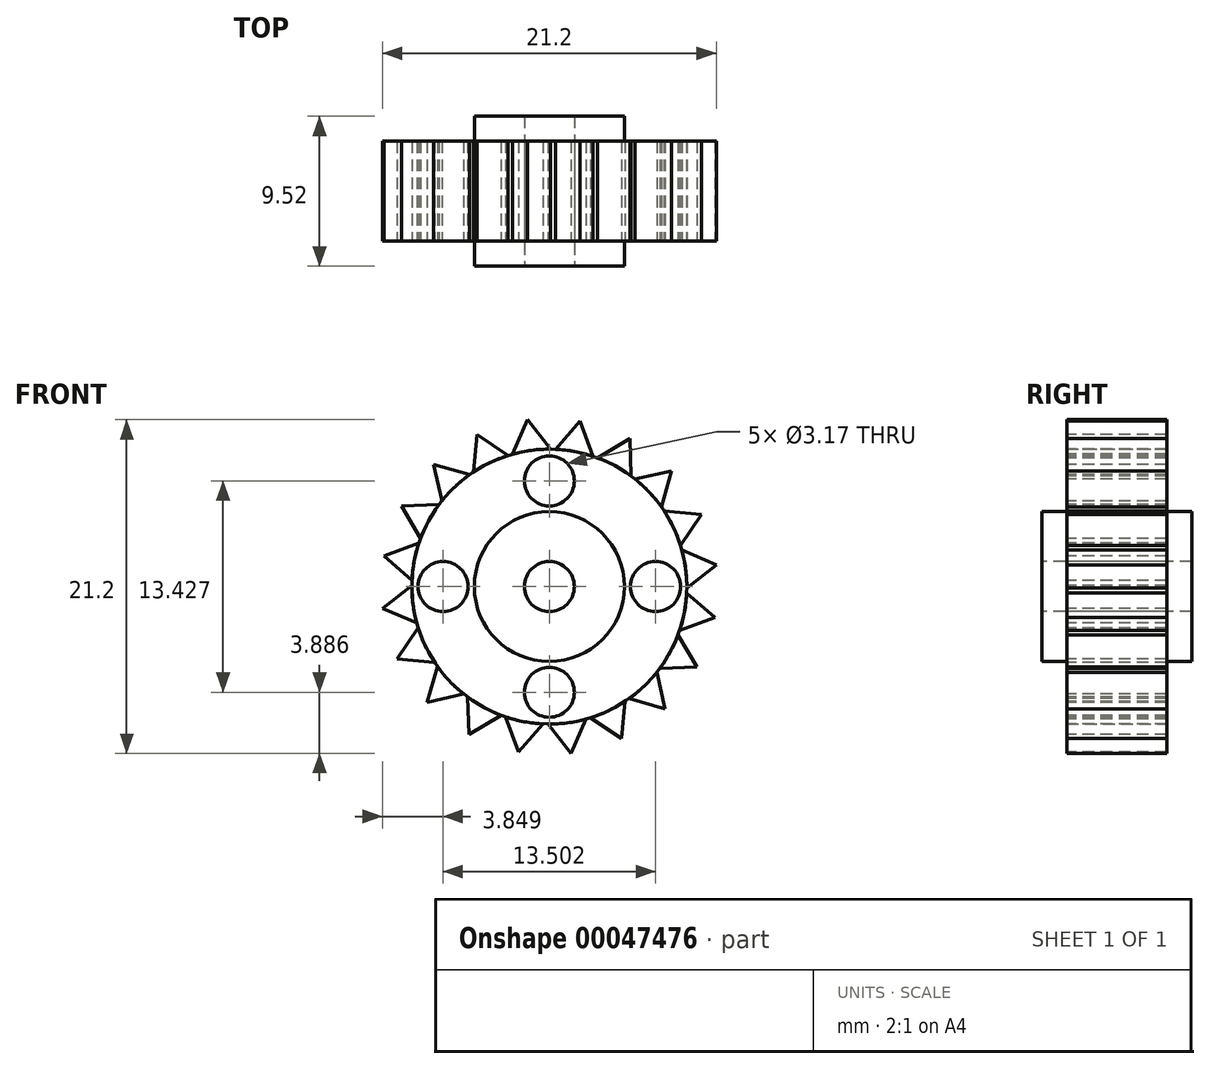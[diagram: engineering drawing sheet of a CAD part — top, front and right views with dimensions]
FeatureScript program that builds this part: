
annotation { "Feature Type Name" : "Feature", "Feature Type Description" : "" }
export const myFeature = defineFeature(function(context is Context, id is Id, definition is map)
    precondition{}
    {
        {
            var Q0;
            Q0=qCreatedBy(makeId("Front.planeOp"),FACE);
            var sketch = newSketch(context, id + "F0", { "sketchPlane" : qUnion([Q0])});
            skCircle(sketch, "E0", {"center": v(0, 0) * mm, "radius": 8.73 * mm});
            skSolve(sketch);
        }
        {
            var Q0;
            Q0=makeQuery(id+"F0.imprint","IMPRINT",FACE,{"disambiguationData":[TD([[makeQuery(id+"F0.imprint","IMPRINT",EDGE,{"derivedFrom":sQuery(id+"F0.wireOp",EDGE,"E0")}),1.0]])]});
            extrude(context, id + "F1", {"entities" : qUnion([Q0]), "depth" : 6.35 * mm, "symmetric" : true});
        }
        {
            var Q0;
            Q0=makeQuery(id+"F1.opExtrude","CAP_FACE",FACE,{"disambiguationData":[OSD([sQuery(id+"F0.wireOp",EDGE,"E0")])],"isStart":false});
            var sketch = newSketch(context, id + "F2", { "sketchPlane" : qUnion([Q0])});
            skCircle(sketch, "E1", {"center": v(0, 0) * mm, "radius": 4.76 * mm});
            skSolve(sketch);
        }
        {
            var Q0;
            Q0=makeQuery(id+"F2.imprint","IMPRINT",FACE,{"disambiguationData":[TD([[makeQuery(id+"F2.imprint","IMPRINT",EDGE,{"derivedFrom":sQuery(id+"F2.wireOp",EDGE,"E1")}),1.0]])]});
            extrude(context, id + "F3", {"entities" : qUnion([Q0]), "operationType" : NewBodyOperationType.ADD, "depth" : 1.59 * mm});
        }
        {
            var Q0;
            Q0=makeQuery(id+"F3.opExtrude","CAP_FACE",FACE,{"disambiguationData":[OSD([sQuery(id+"F2.wireOp",EDGE,"E1")])],"isStart":false});
            var sketch = newSketch(context, id + "F4", { "sketchPlane" : qUnion([Q0])});
            skCircle(sketch, "E2", {"center": v(0, 0) * mm, "radius": 1.59 * mm});
            skSolve(sketch);
        }
        {
            var Q0;
            Q0=makeQuery(id+"F4.imprint","IMPRINT",FACE,{"disambiguationData":[TD([[makeQuery(id+"F4.imprint","IMPRINT",EDGE,{"derivedFrom":sQuery(id+"F4.wireOp",EDGE,"E2")}),1.0]])]});
            extrude(context, id + "F5", {"entities" : qUnion([Q0]), "operationType" : NewBodyOperationType.REMOVE, "endBound" : BoundingType.THROUGH_ALL, "oppositeDirection" : true, "depth" : 25.4 * mm});
        }
        {
            var Q0;
            Q0=makeQuery(id+"F1.opExtrude","CAP_FACE",FACE,{"disambiguationData":[OSD([sQuery(id+"F0.wireOp",EDGE,"E0")])],"isStart":false});
            var sketch = newSketch(context, id + "F6", { "sketchPlane" : qUnion([Q0])});
            skCircle(sketch, "E3", {"center": v(0, 6.71) * mm, "radius": 1.59 * mm});
            skCircle(sketch, "E4.MirrorC", {"center": v(0, -6.71) * mm, "radius": 1.59 * mm});
            skCircle(sketch, "E5", {"center": v(-6.75, 0) * mm, "radius": 1.59 * mm});
            skCircle(sketch, "E6.MirrorC", {"center": v(6.75, 0) * mm, "radius": 1.59 * mm});
            skSolve(sketch);
        }
        {
            var Q0;
            Q0 = qSketchRegion(id + "F6", true);
            extrude(context, id + "F7", {"entities" : qUnion([Q0]), "operationType" : NewBodyOperationType.REMOVE, "endBound" : BoundingType.THROUGH_ALL, "oppositeDirection" : true, "depth" : 25.4 * mm});
        }
        {
            var Q0;
            Q0=makeQuery(id+"F1.opExtrude","SWEPT_BODY",BODY,{"disambiguationData":[OSD([sQuery(id+"F0.wireOp",EDGE,"E0")])]});
            var Q1;
            Q1=qCreatedBy(makeId("Front.planeOp"),FACE);
            mirror(context, id + "F8", {"operationType" : NewBodyOperationType.ADD, "entities" : qUnion([Q0]), "mirrorPlane" : qUnion([Q1])});
        }
        {
            var Q0;
            Q0=makeQuery(id+"F1.opExtrude","CAP_FACE",FACE,{"disambiguationData":[OSD([sQuery(id+"F0.wireOp",EDGE,"E0")])],"isStart":false});
            var sketch = newSketch(context, id + "F9", { "sketchPlane" : qUnion([Q0])});
            skLineSegment(sketch, "E7", {"start": v(-2.32, 8.42) * mm, "end": v(-1.38, 10.6) * mm});
            skLineSegment(sketch, "E8", {"start": v(-1.38, 10.6) * mm, "end": v(0.09, 8.73) * mm});
            skArc(sketch, "E9.trimOffspring", {"start": v(0.09, 8.73) * mm, "mid": v(-1.13, 8.66) * mm, "end": v(-2.32, 8.42) * mm});
            skSolve(sketch);
        }
        {
            var Q0;
            Q0 = qSketchRegion(id + "F9", true);
            var Q1;
            Q1=makeQuery(id+"F1.opExtrude","CAP_FACE",FACE,{"disambiguationData":[OSD([sQuery(id+"F0.wireOp",EDGE,"E0")])],"isStart":true});
            extrude(context, id + "F10", {"entities" : qUnion([Q0]), "endBound" : BoundingType.UP_TO_SURFACE, "oppositeDirection" : true, "endBoundEntityFace" : qUnion([Q1]), "depth" : 25.4 * mm});
        }
        {
            var Q0;
            Q0=makeQuery(id+"F10.opExtrude","SWEPT_BODY",BODY,{"disambiguationData":[OSD([sQuery(id+"F9.wireOp",EDGE,"E7"),sQuery(id+"F9.wireOp",EDGE,"E8"),sQuery(id+"F9.wireOp",EDGE,"E9.trimOffspring")])]});
            var Q1;
            Q1=makeQuery(id+"F1.opExtrude","CAP_EDGE",EDGE,{"disambiguationData":[OSD([sQuery(id+"F0.wireOp",EDGE,"E0")])],"isStart":false});
            circularPattern(context, id + "F11", {"entities" : qUnion([Q0]), "axis" : qUnion([Q1]), "angle" : 360 * degree, "instanceCount" : 20, "equalSpace" : true});
        }
    });
